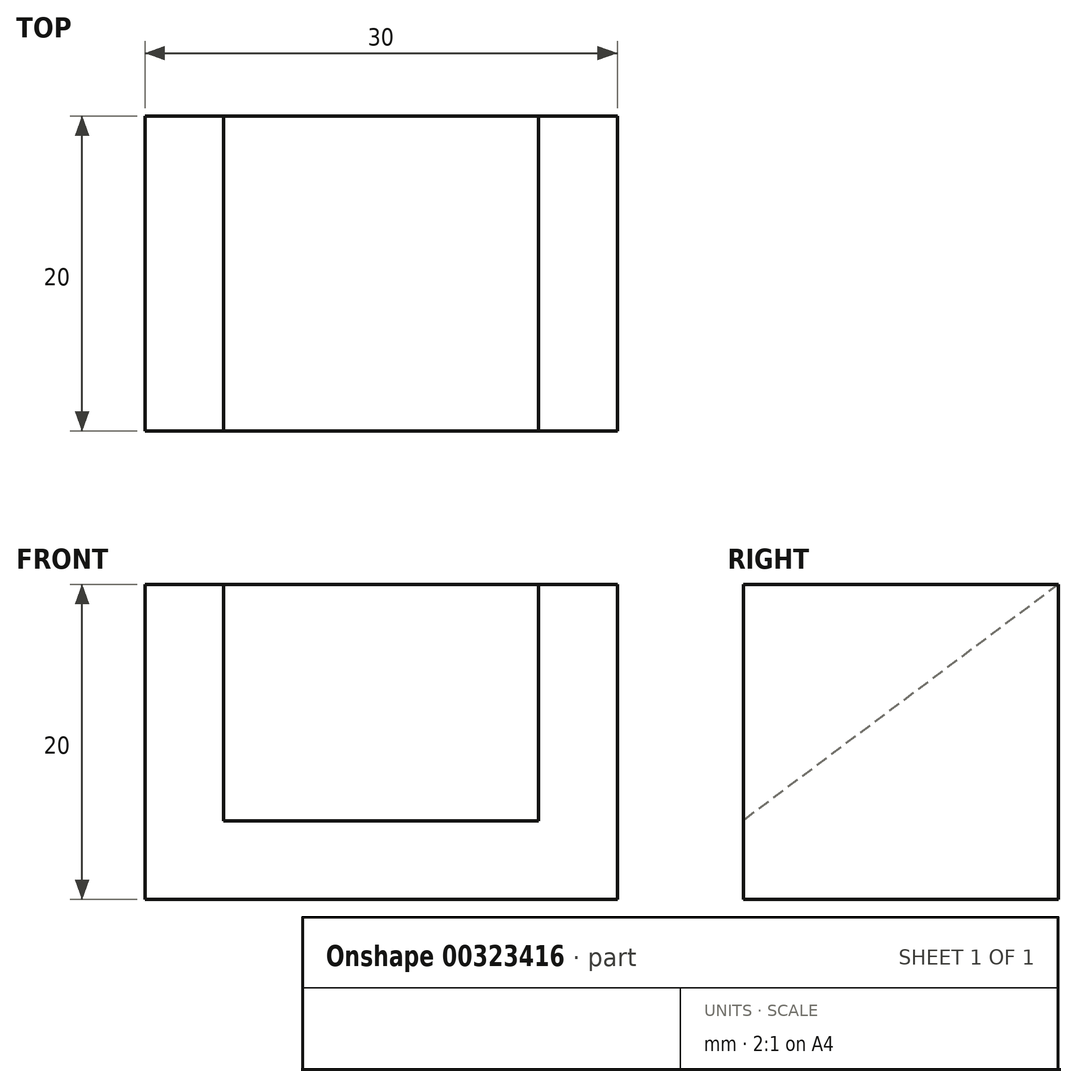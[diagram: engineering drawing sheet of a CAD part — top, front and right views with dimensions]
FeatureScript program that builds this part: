
annotation { "Feature Type Name" : "Feature", "Feature Type Description" : "" }
export const myFeature = defineFeature(function(context is Context, id is Id, definition is map)
    precondition{}
    {
        {
            var Q0;
            Q0=qCreatedBy(makeId("Front.planeOp"),FACE);
            var sketch = newSketch(context, id + "F0", { "sketchPlane" : qUnion([Q0])});
            skLineSegment(sketch, "E0", {"start": v(0, 20) * mm, "end": v(0, 0) * mm});
            skLineSegment(sketch, "E1", {"start": v(0, 0) * mm, "end": v(30, 0) * mm});
            skLineSegment(sketch, "E2", {"start": v(30, 0) * mm, "end": v(30, 20) * mm});
            skLineSegment(sketch, "E3", {"start": v(30, 20) * mm, "end": v(25, 20) * mm});
            skLineSegment(sketch, "E4", {"start": v(25, 20) * mm, "end": v(25, 5) * mm});
            skLineSegment(sketch, "E5", {"start": v(25, 5) * mm, "end": v(5, 5) * mm});
            skLineSegment(sketch, "E6", {"start": v(5, 5) * mm, "end": v(5, 20) * mm});
            skLineSegment(sketch, "E7", {"start": v(5, 20) * mm, "end": v(0, 20) * mm});
            skSolve(sketch);
        }
        {
            var Q0;
            Q0=makeQuery(id+"F0.imprint","IMPRINT",FACE,{"disambiguationData":[TD([[makeQuery(id+"F0.imprint","IMPRINT",EDGE,{"derivedFrom":sQuery(id+"F0.wireOp",EDGE,"E0")}),1.0]])]});
            extrude(context, id + "F1", {"entities" : qUnion([Q0]), "depth" : 20 * mm, "symmetric" : true});
        }
        {
            var Q0;
            Q0=makeQuery(id+"F1.opExtrude","SWEPT_FACE",FACE,{"disambiguationData":[OSD([sQuery(id+"F0.wireOp",EDGE,"E6")])]});
            var sketch = newSketch(context, id + "F2", { "sketchPlane" : qUnion([Q0])});
            skLineSegment(sketch, "E8", {"start": v(10, 20) * mm, "end": v(-10, 5) * mm});
            skLineSegment(sketch, "E9", {"start": v(-10, 5) * mm, "end": v(10, 5) * mm});
            skLineSegment(sketch, "E10", {"start": v(10, 5) * mm, "end": v(10, 20) * mm});
            skSolve(sketch);
        }
        {
            var Q0;
            Q0=makeQuery(id+"F2.imprint","IMPRINT",FACE,{"disambiguationData":[TD([[makeQuery(id+"F2.imprint","IMPRINT",EDGE,{"derivedFrom":sQuery(id+"F2.wireOp",EDGE,"E8")}),1.0]])]});
            extrude(context, id + "F3", {"entities" : qUnion([Q0]), "operationType" : NewBodyOperationType.ADD, "endBound" : BoundingType.UP_TO_NEXT, "depth" : 25 * mm});
        }
    });
